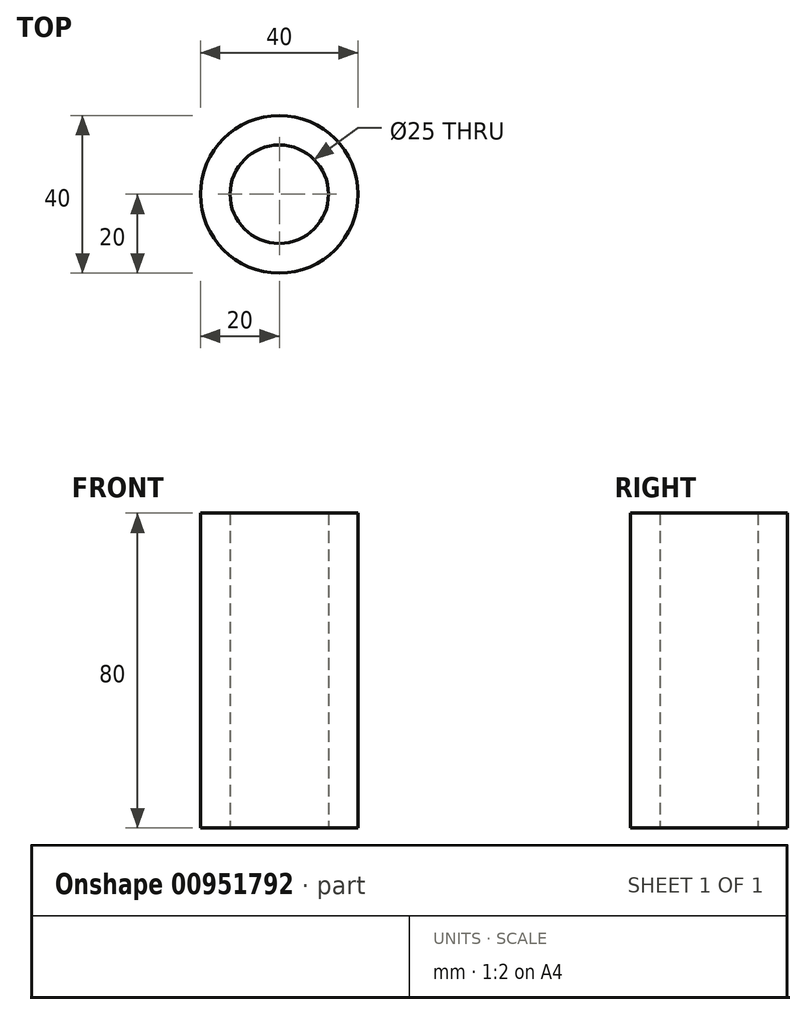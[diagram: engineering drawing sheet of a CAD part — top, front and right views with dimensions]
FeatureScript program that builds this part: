
annotation { "Feature Type Name" : "Feature", "Feature Type Description" : "" }
export const myFeature = defineFeature(function(context is Context, id is Id, definition is map)
    precondition{}
    {
        {
            var Q0;
            Q0=qCreatedBy(makeId("Top.planeOp"),FACE);
            var sketch = newSketch(context, id + "F0", { "sketchPlane" : qUnion([Q0])});
            skCircle(sketch, "E0", {"center": v(0, 0) * mm, "radius": 12.5 * mm});
            skCircle(sketch, "E1", {"center": v(0, 0) * mm, "radius": 20 * mm});
            skSolve(sketch);
        }
        {
            var Q0;
            Q0=makeQuery(id+"F0.imprint","IMPRINT",FACE,{"disambiguationData":[TD([[makeQuery(id+"F0.imprint","IMPRINT",EDGE,{"derivedFrom":sQuery(id+"F0.wireOp",EDGE,"E0")}),-1.0]])]});
            extrude(context, id + "F1", {"entities" : qUnion([Q0]), "depth" : 80 * mm, "offsetDistance" : 25 * mm});
        }
    });
